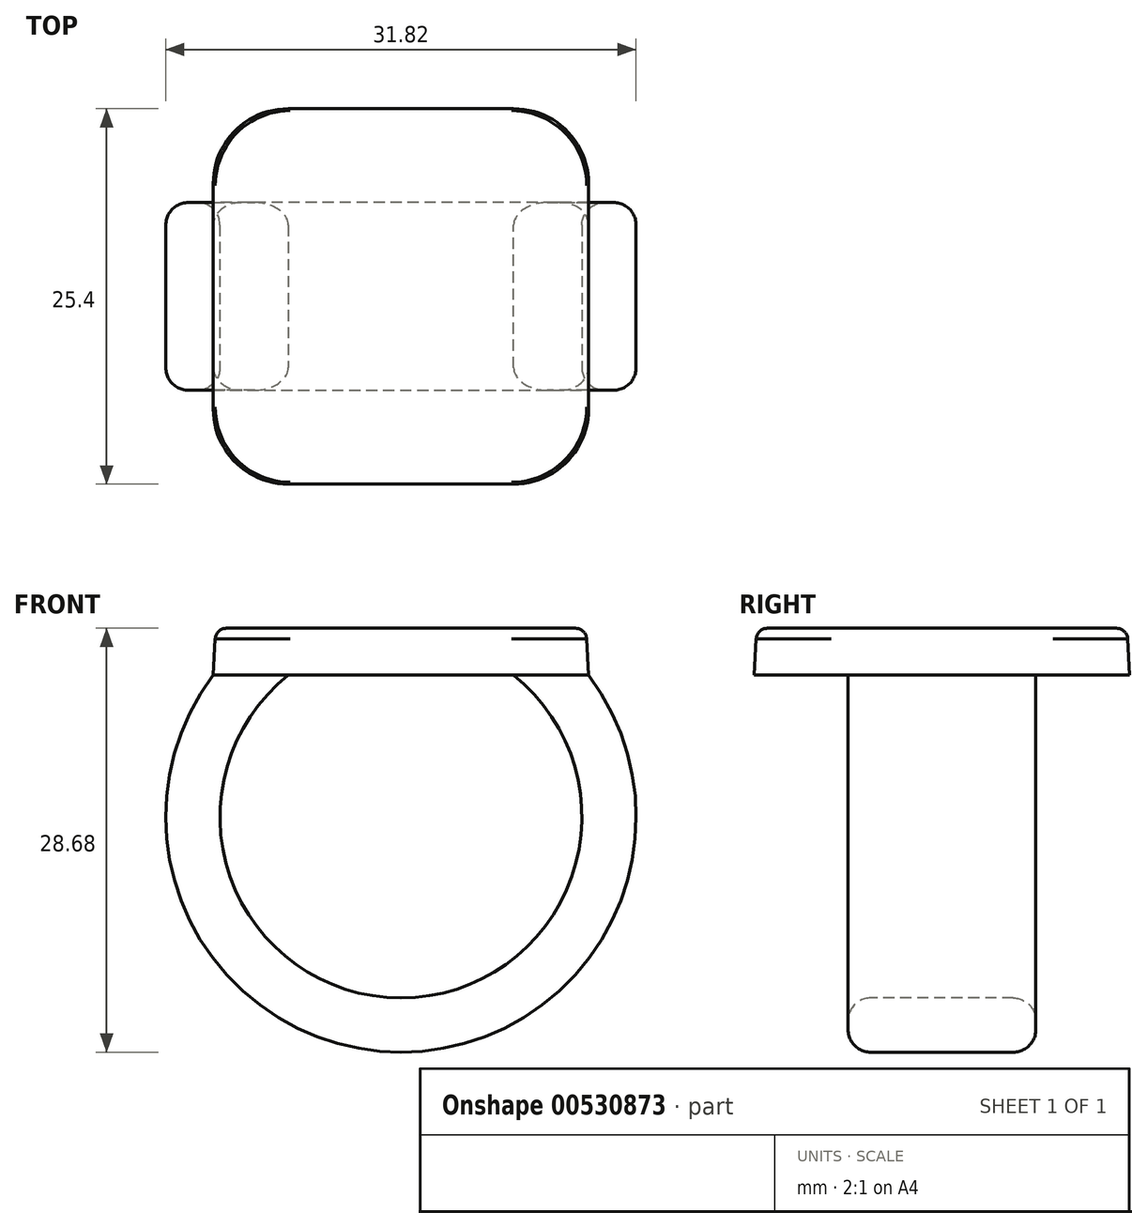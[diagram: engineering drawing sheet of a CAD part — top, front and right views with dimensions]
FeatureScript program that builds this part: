
annotation { "Feature Type Name" : "Feature", "Feature Type Description" : "" }
export const myFeature = defineFeature(function(context is Context, id is Id, definition is map)
    precondition{}
    {
        {
            var Q0;
            Q0=qCreatedBy(makeId("Top.planeOp"),FACE);
            var sketch = newSketch(context, id + "F0", { "sketchPlane" : qUnion([Q0])});
            skLineSegment(sketch, "E0.bottom", {"start": v(12.7, 12.7) * mm, "end": v(-12.7, 12.7) * mm});
            skLineSegment(sketch, "E0.top", {"start": v(12.7, -12.7) * mm, "end": v(-12.7, -12.7) * mm});
            skLineSegment(sketch, "E0.left", {"start": v(12.7, 12.7) * mm, "end": v(12.7, -12.7) * mm});
            skLineSegment(sketch, "E0.right", {"start": v(-12.7, 12.7) * mm, "end": v(-12.7, -12.7) * mm});
            skPoint(sketch, "E0.middle", {"position": v(0, 0) * mm});
            skSolve(sketch);
        }
        {
            var Q0;
            Q0 = qSketchRegion(id + "F0", true);
            extrude(context, id + "F1", {"entities" : qUnion([Q0]), "depth" : 3.17 * mm, "offsetDistance" : 25.4 * mm, "hasDraft" : true, "draftAngle" : 3 * degree, "draftPullDirection" : true});
        }
        {
            var Q0;
            Q0=qCreatedBy(makeId("Front.planeOp"),FACE);
            var sketch = newSketch(context, id + "F2", { "sketchPlane" : qUnion([Q0])});
            skArc(sketch, "E1", {"start": v(-10.16, 0) * mm, "mid": v(0, -23.56) * mm, "end": v(10.16, 0) * mm});
            skSolve(sketch);
        }
        {
            var Q0;
            Q0=makeQuery(id+"F1.opExtrude","CAP_FACE",FACE,{"disambiguationData":[OSD([sQuery(id+"F0.wireOp",EDGE,"E0.bottom"),sQuery(id+"F0.wireOp",EDGE,"E0.top"),sQuery(id+"F0.wireOp",EDGE,"E0.left"),sQuery(id+"F0.wireOp",EDGE,"E0.right")])],"isStart":true});
            var sketch = newSketch(context, id + "F3", { "sketchPlane" : qUnion([Q0])});
            skLineSegment(sketch, "E2.bottom", {"start": v(-7.62, -6.35) * mm, "end": v(-12.7, -6.35) * mm});
            skLineSegment(sketch, "E2.top", {"start": v(-7.62, 6.35) * mm, "end": v(-12.7, 6.35) * mm});
            skLineSegment(sketch, "E2.left", {"start": v(-7.62, -6.35) * mm, "end": v(-7.62, 6.35) * mm});
            skLineSegment(sketch, "E2.right", {"start": v(-12.7, -6.35) * mm, "end": v(-12.7, 6.35) * mm});
            skPoint(sketch, "E2.middle", {"position": v(-10.16, 0) * mm});
            skSolve(sketch);
        }
        {
            var Q0;
            Q0 = qSketchRegion(id + "F3", true);
            var Q1;
            Q1 = qConstructionFilter(qBodyType(qCreatedBy(id + "F2" ,EDGE), BodyType.WIRE), ConstructionObject.NO);
            sweep(context, id + "F4", {"operationType" : NewBodyOperationType.ADD, "profiles" : qUnion([Q0]), "path" : qUnion([Q1])});
        }
        {
            var Q0;
            Q0=qCreatedBy(makeId("Front.planeOp"),FACE);
            var sketch = newSketch(context, id + "F5", { "sketchPlane" : qUnion([Q0])});
            skLineSegment(sketch, "E3.0", {"start": v(10.16, 0) * mm, "end": v(7.62, 0) * mm});
            skLineSegment(sketch, "E3.1", {"start": v(10.01, -2.54) * mm, "end": v(10.16, 0) * mm});
            skArc(sketch, "E3.2", {"start": v(10.01, -2.54) * mm, "mid": v(8.9, -1.18) * mm, "end": v(7.62, 0) * mm});
            skPoint(sketch, "E4.orphan", {"position": v(12.7, 0) * mm});
            skPoint(sketch, "E5.orphan", {"position": v(-12.7, 0) * mm});
            skPoint(sketch, "E6.orphan", {"position": v(-7.62, 0) * mm});
            skSolve(sketch);
        }
        {
            var Q0;
            Q0 = qSketchRegion(id + "F5", true);
            var Q1;
            Q1=makeQuery(id+"F4.opSweep","SWEPT_FACE",FACE,{"disambiguationData":[OSD([sQuery(id+"F2.wireOp",EDGE,"E1"),sQuery(id+"F3.wireOp",EDGE,"E2.top")])]});
            var Q2;
            Q2=makeQuery(id+"F4.opSweep","SWEPT_FACE",FACE,{"disambiguationData":[OSD([sQuery(id+"F2.wireOp",EDGE,"E1"),sQuery(id+"F3.wireOp",EDGE,"E2.bottom")])]});
            extrude(context, id + "F6", {"entities" : qUnion([Q0]), "operationType" : NewBodyOperationType.ADD, "endBound" : BoundingType.UP_TO_SURFACE, "depth" : 25.4 * mm, "endBoundEntityFace" : qUnion([Q1]), "offsetDistance" : 25.4 * mm, "hasSecondDirection" : true, "secondDirectionBound" : SecondDirectionBoundingType.UP_TO_SURFACE, "secondDirectionOppositeDirection" : true, "secondDirectionDepth" : 25.4 * mm, "secondDirectionBoundEntityFace" : qUnion([Q2])});
        }
        {
            var Q0;
            Q0=makeQuery(id+"F1.opExtrude","SWEPT_EDGE",EDGE,{"disambiguationData":[OSD([sQuery(id+"F0.wireOp",EDGE,"E0.top"),sQuery(id+"F0.wireOp",EDGE,"E0.left")])]});
            var Q1;
            Q1=makeQuery(id+"F1.opExtrude","SWEPT_EDGE",EDGE,{"disambiguationData":[OSD([sQuery(id+"F0.wireOp",EDGE,"E0.bottom"),sQuery(id+"F0.wireOp",EDGE,"E0.left")])]});
            var Q2;
            Q2=makeQuery(id+"F1.opExtrude","SWEPT_EDGE",EDGE,{"disambiguationData":[OSD([sQuery(id+"F0.wireOp",EDGE,"E0.bottom"),sQuery(id+"F0.wireOp",EDGE,"E0.right")])]});
            var Q3;
            Q3=makeQuery(id+"F1.opExtrude","SWEPT_EDGE",EDGE,{"disambiguationData":[OSD([sQuery(id+"F0.wireOp",EDGE,"E0.top"),sQuery(id+"F0.wireOp",EDGE,"E0.right")])]});
            fillet(context, id + "F7", {"entities" : qUnion([Q0, Q1, Q2, Q3]), "radius" : 5.08 * mm, "tangentPropagation" : true, "allowEdgeOverflow" : false});
        }
        {
            var Q0;
            Q0=makeQuery(id+"F4.opSweep","SWEPT_EDGE",EDGE,{"disambiguationData":[OSD([sQuery(id+"F0.wireOp",EDGE,"E0.right"),sQuery(id+"F2.wireOp",EDGE,"E1"),sQuery(id+"F3.wireOp",EDGE,"E2.top"),sQuery(id+"F3.wireOp",EDGE,"E2.right")])]});
            var Q1;
            Q1=makeQuery(id+"F4.opSweep","SWEPT_EDGE",EDGE,{"disambiguationData":[OSD([sQuery(id+"F0.wireOp",EDGE,"E0.right"),sQuery(id+"F2.wireOp",EDGE,"E1"),sQuery(id+"F3.wireOp",EDGE,"E2.bottom"),sQuery(id+"F3.wireOp",EDGE,"E2.right")])]});
            var Q2;
            {var subQ0=sQuery(id+"F3.wireOp",EDGE,"E2.bottom");var subQ1=sQuery(id+"F2.wireOp",EDGE,"E1");Q2=makeQuery(id+"F6.boolean.opBoolean","MERGE",EDGE,{"derivedFrom":[makeQuery(id+"F4.opSweep","SWEPT_EDGE",EDGE,{"disambiguationData":[OSD([subQ1,subQ0,sQuery(id+"F3.wireOp",EDGE,"E2.left")])]}),makeQuery(id+"F6.opExtrude","TWEAK_EDGE",EDGE,{"derivedFrom":[makeQuery(id+"F4.opSweep","SWEPT_FACE",FACE,{"disambiguationData":[OSD([subQ1,subQ0])]}),makeQuery(id+"F5.imprint","IMPRINT",EDGE,{"derivedFrom":sQuery(id+"F5.wireOp",EDGE,"E3.2")})]})]});}
            var Q3;
            {var subQ0=sQuery(id+"F3.wireOp",EDGE,"E2.top");var subQ1=sQuery(id+"F2.wireOp",EDGE,"E1");Q3=makeQuery(id+"F6.boolean.opBoolean","MERGE",EDGE,{"derivedFrom":[makeQuery(id+"F4.opSweep","SWEPT_EDGE",EDGE,{"disambiguationData":[OSD([subQ1,subQ0,sQuery(id+"F3.wireOp",EDGE,"E2.left")])]}),makeQuery(id+"F6.opExtrude","TWEAK_EDGE",EDGE,{"derivedFrom":[makeQuery(id+"F4.opSweep","SWEPT_FACE",FACE,{"disambiguationData":[OSD([subQ1,subQ0])]}),makeQuery(id+"F5.imprint","IMPRINT",EDGE,{"derivedFrom":sQuery(id+"F5.wireOp",EDGE,"E3.2")})]})]});}
            fillet(context, id + "F8", {"entities" : qUnion([Q0, Q1, Q2, Q3]), "radius" : 1.52 * mm, "tangentPropagation" : true, "allowEdgeOverflow" : false});
        }
        {
            var Q0;
            Q0=makeQuery(id+"F1.opExtrude","CAP_FACE",FACE,{"disambiguationData":[OSD([sQuery(id+"F0.wireOp",EDGE,"E0.bottom"),sQuery(id+"F0.wireOp",EDGE,"E0.top"),sQuery(id+"F0.wireOp",EDGE,"E0.left"),sQuery(id+"F0.wireOp",EDGE,"E0.right")])],"isStart":false});
            fillet(context, id + "F9", {"entities" : qUnion([Q0]), "radius" : 0.76 * mm, "tangentPropagation" : true, "allowEdgeOverflow" : false});
        }
    });
